# Revit family: Zumtobel MIRAL FEW
name_source: partatom
category: Lighting Fixtures
revit_build: Autodesk Revit 2016 (Build: 20150220_1215(x64)
units: mm (PartAtom-declared; Revit-internal decimal feet)

## family parameters
Cut with Voids When Loaded = No
Host = Face
Light Source = Yes
OmniClass Number = 23.80.70.11
OmniClass Title = Luminaries for Internal Lighting
Part Type = Normal
Room Calculation Point = No
Round Connector Dimension = Use Diameter
Shared = No

## types (12) — shared parameters
Assembly Code = D5020200
Color Filter = 16777215
Description = Recessed luminaires with asymm. optic
Dimming Lamp Color Temperature Shift = <None>
Emit Shape Visible in Rendering = No
Height = 85 mm  [stored 0.278871 ft]
Manufacturer = Zumtobel Lighting
Tilt Angle = 90.00°
URL = http://www.zumtobel.com
Voltage = 230 V
zero-valued in all types: Default Elevation

## per-type parameters (varying)
| type | Apparent Load | Emit from Rectangle Length | Emit from Rectangle Width | Lamp | Length | Model | Photometric Web File | T16 | TCL | Width |
| FEW 1/55W TC-L Dimmable | 61 VA | 176 mm | 574 mm  [stored 1.8832 ft] | TC-L | 598 mm  [stored 1.96194 ft] | 42910357 | D22493L5.IES | No | Yes | 200 mm  [stored 0.656168 ft] |
| FEW 1/55W TC-L Electronic | 61 VA | 176 mm | 574 mm  [stored 1.8832 ft] | TC-L | 598 mm  [stored 1.96194 ft] | 42159253 | D22493L5.IES | No | Yes | 200 mm  [stored 0.656168 ft] |
| FEW 1/80W T16 Dimmable | 86 VA | 90 mm | 1474 mm  [stored 4.83596 ft] | T16 | 1498 mm  [stored 4.9147 ft] | 42913164 | D22498U9.IES | Yes | No | 114 mm  [stored 0.374016 ft] |
| FEW 1/80W T16 Electronic | 86 VA | 90 mm | 1474 mm  [stored 4.83596 ft] | T16 | 1498 mm  [stored 4.9147 ft] | 42159257 | D22498U9.IES | Yes | No | 114 mm  [stored 0.374016 ft] |
| FEW 1/54W T16 Dimmable | 58 VA | 90 mm | 1174 mm  [stored 3.85171 ft] | T16 | 1198 mm  [stored 3.93045 ft] | 42910364 | D22498U8.IES | Yes | No | 114 mm  [stored 0.374016 ft] |
| FEW 1/54W T16 Electronic | 58 VA | 90 mm | 1174 mm  [stored 3.85171 ft] | T16 | 1198 mm  [stored 3.93045 ft] | 42159256 | D22498U8.IES | Yes | No | 114 mm  [stored 0.374016 ft] |
| FEW 1/49W T16 Electronic | 53 VA | 90 mm | 1474 mm  [stored 4.83596 ft] | T16 | 1498 mm  [stored 4.9147 ft] | 42181066 | D22497U4.IES | Yes | No | 114 mm  [stored 0.374016 ft] |
| FEW 1/35W T16 Dimmable | 39 VA | 90 mm | 1474 mm  [stored 4.83596 ft] | T16 | 1498 mm  [stored 4.9147 ft] | 42910874 | D22497U4.IES | Yes | No | 114 mm  [stored 0.374016 ft] |
| FEW 1/35W T16 Electronic | 39 VA | 90 mm | 1474 mm  [stored 4.83596 ft] | T16 | 1498 mm  [stored 4.9147 ft] | 42159255 | D22497U4.IES | Yes | No | 114 mm  [stored 0.374016 ft] |
| FEW 1/28W T16 Dimmable | 31 VA | 90 mm | 1174 mm  [stored 3.85171 ft] | T16 | 1198 mm  [stored 3.93045 ft] | 42910757 | D22497U3.IES | Yes | No | 114 mm  [stored 0.374016 ft] |
| FEW 1/28W T16 Electronic | 31 VA | 90 mm | 1174 mm  [stored 3.85171 ft] | T16 | 1198 mm  [stored 3.93045 ft] | 42159254 | D22497U3.IES | Yes | No | 114 mm  [stored 0.374016 ft] |
| FEW LED4400 M600L | 31 VA | 90 mm | 1174 mm  [stored 3.85171 ft] | LED | 1198 mm  [stored 3.93045 ft] | 42183541 | 42183541_(STD_LEO).IES | Yes | No | 114 mm  [stored 0.374016 ft] |

note: [stored X ft] marks values corroborated as IEEE doubles in the binary element streams (Revit-internal decimal feet)

## geometry (parser evidence)
native form markers: Blend x12, Sweep x5
no freeform markers — native parametric forms only
